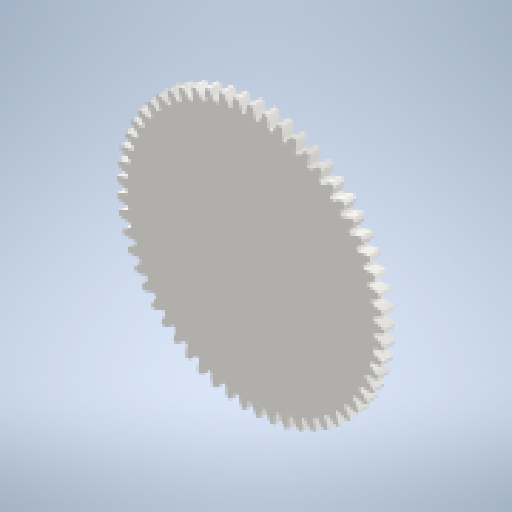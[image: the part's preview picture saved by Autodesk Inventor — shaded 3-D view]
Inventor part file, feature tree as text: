
AUTODESK INVENTOR PART (.ipt)
format: ipt  version: 2023 (Build 270158000, 158)  size: 410,624 bytes
history: native  units: mm (DEFAULTED — no unit token found)
features: plane x3, other x3, sketch x3, extrude x2, projected_geometry x1
ambient origin geometry x8: Origin, YZ Plane, XZ Plane, XY Plane, X Axis, Y Axis, Z Axis, Center Point
bodies: Solid1 (feature_tree)
feature tree (12):
  extrude  "Extrusion1"  Depth=5.0mm TaperAngle=0.0deg
  plane  "Work Plane2"
  plane  "Work Plane8"
  plane  "Work Plane9"
  other  "Spur Gear"
  extrude  "Extrusion2"  Depth=10.0mm TaperAngle=0.0deg
  sketch  "Sketch1"  dims[d0=64.0mm d1=5.0mm d2=0.0mm]
  sketch  "Sketch2"  dims[d3=60.0mm d4=10.0mm d5=0.0mm]
  other  "Srf1"
  sketch  "Sketch3"  dims[d16=40.0mm d17=0.0mm d34=1.047198mm d39=0.0mm d41=0.0mm d43=40.0mm d46=40.0mm d47=0.0mm d48=0.0mm d49=2.32mm d50=7.0mm d51=2.0mm d52=50.0mm d54=360.0deg d56=0.0mm d57=0.0mm d58=5.0mm]
  projected_geometry  "Projected Loop1"
  other  "Pitch Diameter"
